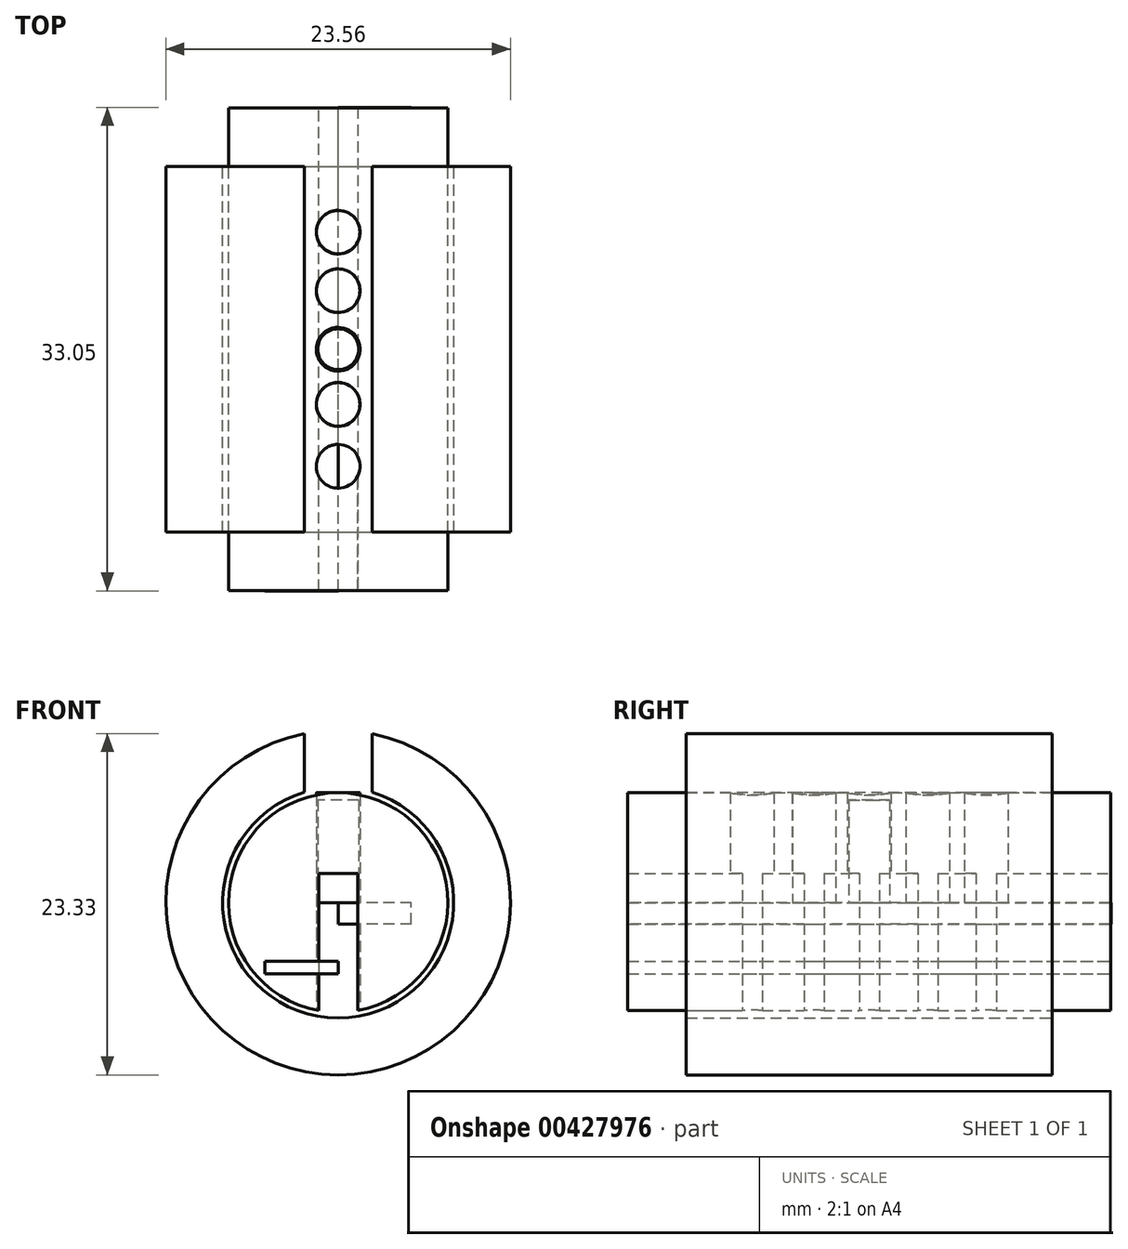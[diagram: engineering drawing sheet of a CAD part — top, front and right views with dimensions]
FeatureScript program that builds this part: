
annotation { "Feature Type Name" : "Feature", "Feature Type Description" : "" }
export const myFeature = defineFeature(function(context is Context, id is Id, definition is map)
    precondition{}
    {
        {
            var Q0;
            Q0=qCreatedBy(makeId("Front.planeOp"),FACE);
            var sketch = newSketch(context, id + "F0", { "sketchPlane" : qUnion([Q0])});
            skCircle(sketch, "E0", {"center": v(0, 0) * mm, "radius": 7.5 * mm});
            skSolve(sketch);
        }
        {
            var Q0;
            Q0 = qSketchRegion(id + "F0", true);
            extrude(context, id + "F1", {"entities" : qUnion([Q0]), "endBound" : BoundingType.SYMMETRIC, "depth" : 33 * mm});
        }
        {
            var Q0;
            Q0=makeQuery(id+"F1.opExtrude","CAP_FACE",FACE,{"disambiguationData":[OSD([sQuery(id+"F0.wireOp",EDGE,"E0")])],"isStart":false});
            var sketch = newSketch(context, id + "F2", { "sketchPlane" : qUnion([Q0])});
            skLineSegment(sketch, "E1", {"start": v(0, -7.5) * mm, "end": v(0, 2) * mm});
            skLineSegment(sketch, "E2.bottom", {"start": v(-1.34, 2) * mm, "end": v(1.34, 2) * mm});
            skLineSegment(sketch, "E2.top", {"start": v(-1.34, -7.5) * mm, "end": v(1.34, -7.5) * mm});
            skLineSegment(sketch, "E2.left", {"start": v(-1.34, 2) * mm, "end": v(-1.34, -7.5) * mm});
            skLineSegment(sketch, "E2.right", {"start": v(1.34, 2) * mm, "end": v(1.34, -7.5) * mm});
            skPoint(sketch, "E2.middle", {"position": v(0, -2.75) * mm});
            skSolve(sketch);
        }
        {
            var Q0;
            {var subQ0=sQuery(id+"F2.wireOp",EDGE,"E2.top");var subQ3=sQuery(id+"F2.wireOp",EDGE,"E2.left");var subQ4=makeQuery(id+"F2.imprint","INTERSECT",VERTEX,{"derivedFrom":[subQ0,subQ3]});Q0=makeQuery(id+"F2.imprint","IMPRINT",FACE,{"disambiguationData":[TD([[makeQuery(id+"F2.imprint","IMPRINT",EDGE,{"disambiguationData":[TD([[subQ4,1.0]])],"derivedFrom":subQ3}),1.0]])]});}
            var Q1;
            {var subQ0=sQuery(id+"F2.wireOp",EDGE,"E2.top");var subQ3=sQuery(id+"F2.wireOp",EDGE,"E2.right");var subQ4=makeQuery(id+"F2.imprint","INTERSECT",VERTEX,{"derivedFrom":[subQ0,subQ3]});Q1=makeQuery(id+"F2.imprint","IMPRINT",FACE,{"disambiguationData":[TD([[makeQuery(id+"F2.imprint","IMPRINT",EDGE,{"disambiguationData":[TD([[subQ4,1.0]])],"derivedFrom":subQ3}),-1.0]])]});}
            var Q2;
            {var subQ0=sQuery(id+"F2.wireOp",EDGE,"E1");Q2=makeQuery(id+"F2.imprint","IMPRINT",FACE,{"disambiguationData":[TD([[makeQuery(id+"F2.imprint","IMPRINT",EDGE,{"derivedFrom":subQ0}),1.0]])]});}
            var Q3;
            {var subQ0=sQuery(id+"F2.wireOp",EDGE,"E1");Q3=makeQuery(id+"F2.imprint","IMPRINT",FACE,{"disambiguationData":[TD([[makeQuery(id+"F2.imprint","IMPRINT",EDGE,{"derivedFrom":subQ0}),-1.0]])]});}
            extrude(context, id + "F3", {"entities" : qUnion([Q0, Q1, Q2, Q3]), "operationType" : NewBodyOperationType.REMOVE, "endBound" : BoundingType.SYMMETRIC, "depth" : 100 * mm});
        }
        {
            var Q0;
            Q0=qCreatedBy(makeId("Top.planeOp"),FACE);
            var sketch = newSketch(context, id + "F4", { "sketchPlane" : qUnion([Q0])});
            skLineSegment(sketch, "E3", {"start": v(0, 0) * mm, "end": v(0, 10.5) * mm});
            skLineSegment(sketch, "E4", {"start": v(0, 10.5) * mm, "end": v(0, -10.5) * mm});
            skCircle(sketch, "E5", {"center": v(0, 0) * mm, "radius": 1.5 * mm});
            skCircle(sketch, "E6", {"center": v(0, 4) * mm, "radius": 1.5 * mm});
            skCircle(sketch, "E7", {"center": v(0, 8) * mm, "radius": 1.5 * mm});
            skCircle(sketch, "E8", {"center": v(0, -3.77) * mm, "radius": 1.5 * mm});
            skCircle(sketch, "E9", {"center": v(0, -8) * mm, "radius": 1.5 * mm});
            skSolve(sketch);
        }
        {
            var Q0;
            Q0 = qSketchRegion(id + "F4", true);
            extrude(context, id + "F5", {"entities" : qUnion([Q0]), "operationType" : NewBodyOperationType.REMOVE, "endBound" : BoundingType.SYMMETRIC, "depth" : 100 * mm});
        }
        {
            var Q0;
            Q0=qCreatedBy(makeId("Top.planeOp"),FACE);
            var sketch = newSketch(context, id + "F6", { "sketchPlane" : qUnion([Q0])});
            skCircle(sketch, "E10", {"center": v(0, 0) * mm, "radius": 1.4 * mm});
            skSolve(sketch);
        }
        {
            var Q0;
            Q0=qCreatedBy(makeId("Right.planeOp"),FACE);
            var sketch = newSketch(context, id + "F7", { "sketchPlane" : qUnion([Q0])});
            skLineSegment(sketch, "E11.bottom", {"start": v(-16.49, 0) * mm, "end": v(16.53, 0) * mm});
            skLineSegment(sketch, "E11.top", {"start": v(-16.49, -1.47) * mm, "end": v(16.53, -1.47) * mm});
            skLineSegment(sketch, "E11.left", {"start": v(-16.49, 0) * mm, "end": v(-16.49, -1.47) * mm});
            skLineSegment(sketch, "E11.right", {"start": v(16.53, 0) * mm, "end": v(16.53, -1.47) * mm});
            skSolve(sketch);
        }
        {
            var Q0;
            Q0 = qSketchRegion(id + "F7", true);
            extrude(context, id + "F8", {"entities" : qUnion([Q0]), "operationType" : NewBodyOperationType.ADD, "depth" : 5 * mm});
        }
        {
            var Q0;
            Q0 = qSketchRegion(id + "F6", true);
            extrude(context, id + "F9", {"entities" : qUnion([Q0]), "depth" : 7 * mm});
        }
        {
            var Q0;
            Q0=qCreatedBy(makeId("Top.planeOp"),FACE);
            var sketch = newSketch(context, id + "F10", { "sketchPlane" : qUnion([Q0])});
            skCircle(sketch, "E12", {"center": v(0, -3.77) * mm, "radius": 1.49 * mm});
            skPoint(sketch, "E12.first.point", {"position": v(1.03, -2.7) * mm});
            skPoint(sketch, "E12.second.point", {"position": v(1.45, -3.45) * mm});
            skPoint(sketch, "E12.third.point", {"position": v(-1.47, -3.57) * mm});
            skSolve(sketch);
        }
        {
            var Q0;
            Q0 = qSketchRegion(id + "F10", true);
            extrude(context, id + "F11", {"entities" : qUnion([Q0]), "depth" : 8.5 * mm});
        }
        {
            var Q0;
            Q0=qCreatedBy(makeId("Top.planeOp"),FACE);
            var sketch = newSketch(context, id + "F12", { "sketchPlane" : qUnion([Q0])});
            skCircle(sketch, "E13", {"center": v(0, 4) * mm, "radius": 1.49 * mm});
            skPoint(sketch, "E13.first.point", {"position": v(1.49, 3.95) * mm});
            skPoint(sketch, "E13.second.point", {"position": v(1.4, 4.53) * mm});
            skPoint(sketch, "E13.third.point", {"position": v(-1.5, 3.92) * mm});
            skSolve(sketch);
        }
        {
            var Q0;
            Q0 = qSketchRegion(id + "F12", true);
            extrude(context, id + "F13", {"entities" : qUnion([Q0]), "depth" : 12 * mm});
        }
        {
            var Q0;
            Q0=qCreatedBy(makeId("Top.planeOp"),FACE);
            var sketch = newSketch(context, id + "F14", { "sketchPlane" : qUnion([Q0])});
            skCircle(sketch, "E14", {"center": v(0, 8) * mm, "radius": 1.48 * mm});
            skPoint(sketch, "E14.first.point", {"position": v(1.47, 8.2) * mm});
            skPoint(sketch, "E14.second.point", {"position": v(0.9, 6.81) * mm});
            skPoint(sketch, "E14.third.point", {"position": v(-1.1, 7) * mm});
            skSolve(sketch);
        }
        {
            var Q0;
            Q0 = qSketchRegion(id + "F14", true);
            extrude(context, id + "F15", {"entities" : qUnion([Q0]), "depth" : 9 * mm});
        }
        {
            var Q0;
            Q0=qCreatedBy(makeId("Right.planeOp"),FACE);
            var sketch = newSketch(context, id + "F16", { "sketchPlane" : qUnion([Q0])});
            skLineSegment(sketch, "E15.bottom", {"start": v(-16.52, -4) * mm, "end": v(16.48, -4) * mm});
            skLineSegment(sketch, "E15.top", {"start": v(-16.52, -4.86) * mm, "end": v(16.48, -4.86) * mm});
            skLineSegment(sketch, "E15.left", {"start": v(-16.52, -4) * mm, "end": v(-16.52, -4.86) * mm});
            skLineSegment(sketch, "E15.right", {"start": v(16.48, -4) * mm, "end": v(16.48, -4.86) * mm});
            skSolve(sketch);
        }
        {
            var Q0;
            Q0 = qSketchRegion(id + "F16", true);
            extrude(context, id + "F17", {"entities" : qUnion([Q0]), "operationType" : NewBodyOperationType.ADD, "depth" : -5 * mm});
        }
        {
            var Q0;
            Q0=qCreatedBy(makeId("Front.planeOp"),FACE);
            var sketch = newSketch(context, id + "F18", { "sketchPlane" : qUnion([Q0])});
            skCircle(sketch, "E16", {"center": v(0, 0) * mm, "radius": 7.9 * mm});
            skCircle(sketch, "E17", {"center": v(0, 0) * mm, "radius": 11.78 * mm});
            skSolve(sketch);
        }
        {
            var Q0;
            Q0=makeQuery(id+"F18.imprint","IMPRINT",FACE,{"disambiguationData":[TD([[makeQuery(id+"F18.imprint","IMPRINT",EDGE,{"derivedFrom":sQuery(id+"F18.wireOp",EDGE,"E16")}),-1.0]])]});
            extrude(context, id + "F19", {"entities" : qUnion([Q0]), "endBound" : BoundingType.SYMMETRIC, "depth" : 25 * mm});
        }
        {
            var Q0;
            Q0=qCreatedBy(makeId("Top.planeOp"),FACE);
            cPlane(context, id + "F20", {"entities" : qUnion([Q0]), "cplaneType" : CPlaneType.OFFSET, "offset" : 7.5 * mm, "width" : 150 * mm, "height" : 150 * mm});
        }
        {
            var Q0;
            Q0=qCreatedBy(id+"F20.planeOp",FACE);
            var sketch = newSketch(context, id + "F21", { "sketchPlane" : qUnion([Q0])});
            skLineSegment(sketch, "E18.bottom", {"start": v(-2.32, 13.95) * mm, "end": v(2.32, 13.95) * mm});
            skLineSegment(sketch, "E18.top", {"start": v(-2.32, -13.95) * mm, "end": v(2.32, -13.95) * mm});
            skLineSegment(sketch, "E18.left", {"start": v(-2.32, 13.95) * mm, "end": v(-2.32, -13.95) * mm});
            skLineSegment(sketch, "E18.right", {"start": v(2.32, 13.95) * mm, "end": v(2.32, -13.95) * mm});
            skPoint(sketch, "E18.middle", {"position": v(0, 0) * mm});
            skSolve(sketch);
        }
        {
            var Q0;
            Q0 = qSketchRegion(id + "F21", true);
            extrude(context, id + "F22", {"entities" : qUnion([Q0]), "operationType" : NewBodyOperationType.REMOVE, "oppositeDirection" : true, "depth" : -25 * mm});
        }
    });
